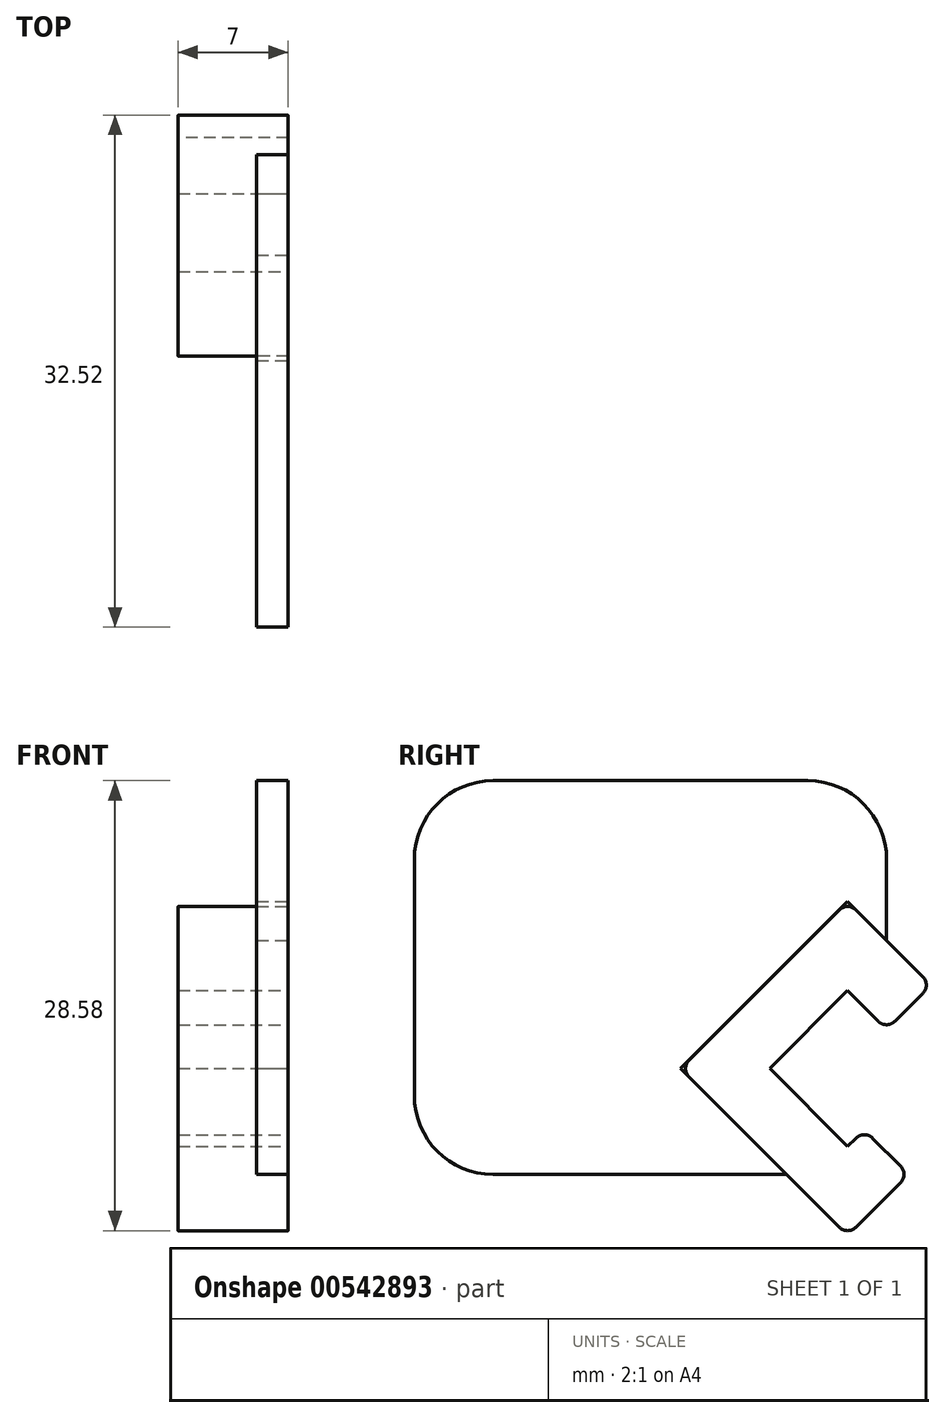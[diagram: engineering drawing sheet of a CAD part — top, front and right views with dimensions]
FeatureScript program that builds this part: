
annotation { "Feature Type Name" : "Feature", "Feature Type Description" : "" }
export const myFeature = defineFeature(function(context is Context, id is Id, definition is map)
    precondition{}
    {
        {
            var Q0;
            Q0=qCreatedBy(makeId("Right.planeOp"),FACE);
            var sketch = newSketch(context, id + "F0", { "sketchPlane" : qUnion([Q0])});
            skLineSegment(sketch, "E0.bottom", {"start": v(0, 7) * mm, "end": v(-4.95, 11.96) * mm});
            skLineSegment(sketch, "E0.top", {"start": v(2.47, 14.43) * mm, "end": v(0, 16.9) * mm});
            skLineSegment(sketch, "E0.left", {"start": v(0, 7) * mm, "end": v(1.06, 8.07) * mm});
            skLineSegment(sketch, "E0.right", {"start": v(-4.95, 11.96) * mm, "end": v(0, 16.9) * mm});
            skLineSegment(sketch, "E1.bottom", {"start": v(-10.6, 11.96) * mm, "end": v(0, 1.35) * mm});
            skLineSegment(sketch, "E1.top", {"start": v(0, 22.56) * mm, "end": v(5.3, 17.26) * mm});
            skLineSegment(sketch, "E1.left", {"start": v(-10.6, 11.96) * mm, "end": v(0, 22.56) * mm});
            skLineSegment(sketch, "E1.right", {"start": v(0, 1.35) * mm, "end": v(3.89, 5.24) * mm});
            skLineSegment(sketch, "E2", {"start": v(5.3, 17.26) * mm, "end": v(2.47, 14.43) * mm});
            skLineSegment(sketch, "E3", {"start": v(1.06, 8.07) * mm, "end": v(3.89, 5.24) * mm});
            skLineSegment(sketch, "E4", {"start": v(2.47, 14.43) * mm, "end": v(2.47, 30.24) * mm});
            skLineSegment(sketch, "E5", {"start": v(2.47, 30.24) * mm, "end": v(-27.53, 30.24) * mm});
            skLineSegment(sketch, "E6", {"start": v(-27.53, 30.24) * mm, "end": v(-27.53, 5.24) * mm});
            skLineSegment(sketch, "E7", {"start": v(-27.53, 5.24) * mm, "end": v(3.89, 5.24) * mm});
            skSolve(sketch);
        }
        {
            var Q0;
            Q0=makeQuery(id+"F0.imprint","IMPRINT",FACE,{"disambiguationData":[TD([[makeQuery(id+"F0.imprint","IMPRINT",EDGE,{"derivedFrom":sQuery(id+"F0.wireOp",EDGE,"E0.bottom")}),1.0]])]});
            var Q1;
            {var subQ0=sQuery(id+"F0.wireOp",EDGE,"E1.right");Q1=makeQuery(id+"F0.imprint","IMPRINT",FACE,{"disambiguationData":[TD([[makeQuery(id+"F0.imprint","IMPRINT",EDGE,{"derivedFrom":subQ0}),1.0]])]});}
            var Q2;
            {var subQ0=sQuery(id+"F0.wireOp",EDGE,"E2");Q2=makeQuery(id+"F0.imprint","IMPRINT",FACE,{"disambiguationData":[TD([[makeQuery(id+"F0.imprint","IMPRINT",EDGE,{"derivedFrom":subQ0}),-1.0]])]});}
            extrude(context, id + "F1", {"entities" : qUnion([Q0, Q1, Q2]), "oppositeDirection" : true, "depth" : 7 * mm, "offsetDistance" : 25 * mm});
        }
        {
            var Q0;
            {var subQ4=sQuery(id+"F0.wireOp",EDGE,"E1.left");Q0=makeQuery(id+"F0.imprint","IMPRINT",FACE,{"disambiguationData":[TD([[makeQuery(id+"F0.imprint","IMPRINT",EDGE,{"derivedFrom":subQ4}),1.0]])]});}
            extrude(context, id + "F2", {"entities" : qUnion([Q0]), "oppositeDirection" : true, "depth" : 2 * mm, "offsetDistance" : 25 * mm});
        }
        {
            var Q0;
            Q0=makeQuery(id+"F2.opExtrude","SWEPT_EDGE",EDGE,{"disambiguationData":[OSD([sQuery(id+"F0.wireOp",EDGE,"E4"),sQuery(id+"F0.wireOp",EDGE,"E5")])]});
            var Q1;
            Q1=makeQuery(id+"F2.opExtrude","SWEPT_EDGE",EDGE,{"disambiguationData":[OSD([sQuery(id+"F0.wireOp",EDGE,"E5"),sQuery(id+"F0.wireOp",EDGE,"E6")])]});
            var Q2;
            Q2=makeQuery(id+"F2.opExtrude","SWEPT_EDGE",EDGE,{"disambiguationData":[OSD([sQuery(id+"F0.wireOp",EDGE,"E6"),sQuery(id+"F0.wireOp",EDGE,"E7")])]});
            fillet(context, id + "F3", {"entities" : qUnion([Q0, Q1, Q2]), "radius" : 5 * mm, "tangentPropagation" : true, "allowEdgeOverflow" : false});
        }
        {
            var Q0;
            Q0=makeQuery(id+"F1.opExtrude","SWEPT_EDGE",EDGE,{"disambiguationData":[OSD([sQuery(id+"F0.wireOp",EDGE,"E0.top"),sQuery(id+"F0.wireOp",EDGE,"E2"),sQuery(id+"F0.wireOp",EDGE,"E4")])]});
            var Q1;
            Q1=makeQuery(id+"F1.opExtrude","SWEPT_EDGE",EDGE,{"disambiguationData":[OSD([sQuery(id+"F0.wireOp",EDGE,"E0.left"),sQuery(id+"F0.wireOp",EDGE,"E3")])]});
            var Q2;
            Q2=makeQuery(id+"F1.opExtrude","SWEPT_EDGE",EDGE,{"disambiguationData":[OSD([sQuery(id+"F0.wireOp",EDGE,"E1.bottom"),sQuery(id+"F0.wireOp",EDGE,"E1.right")])]});
            var Q3;
            Q3=makeQuery(id+"F1.opExtrude","SWEPT_EDGE",EDGE,{"disambiguationData":[OSD([sQuery(id+"F0.wireOp",EDGE,"E1.right"),sQuery(id+"F0.wireOp",EDGE,"E3"),sQuery(id+"F0.wireOp",EDGE,"E7")])]});
            var Q4;
            Q4=makeQuery(id+"F1.opExtrude","SWEPT_EDGE",EDGE,{"disambiguationData":[OSD([sQuery(id+"F0.wireOp",EDGE,"E1.top"),sQuery(id+"F0.wireOp",EDGE,"E2")])]});
            var Q5;
            Q5=makeQuery(id+"F1.opExtrude","SWEPT_EDGE",EDGE,{"disambiguationData":[OSD([sQuery(id+"F0.wireOp",EDGE,"E1.top"),sQuery(id+"F0.wireOp",EDGE,"E1.left")])]});
            var Q6;
            Q6=makeQuery(id+"F1.opExtrude","SWEPT_EDGE",EDGE,{"disambiguationData":[OSD([sQuery(id+"F0.wireOp",EDGE,"E1.bottom"),sQuery(id+"F0.wireOp",EDGE,"E1.left")])]});
            fillet(context, id + "F4", {"entities" : qUnion([Q0, Q1, Q2, Q3, Q4, Q5, Q6]), "radius" : .75 * mm, "tangentPropagation" : true, "allowEdgeOverflow" : false});
        }
    });
